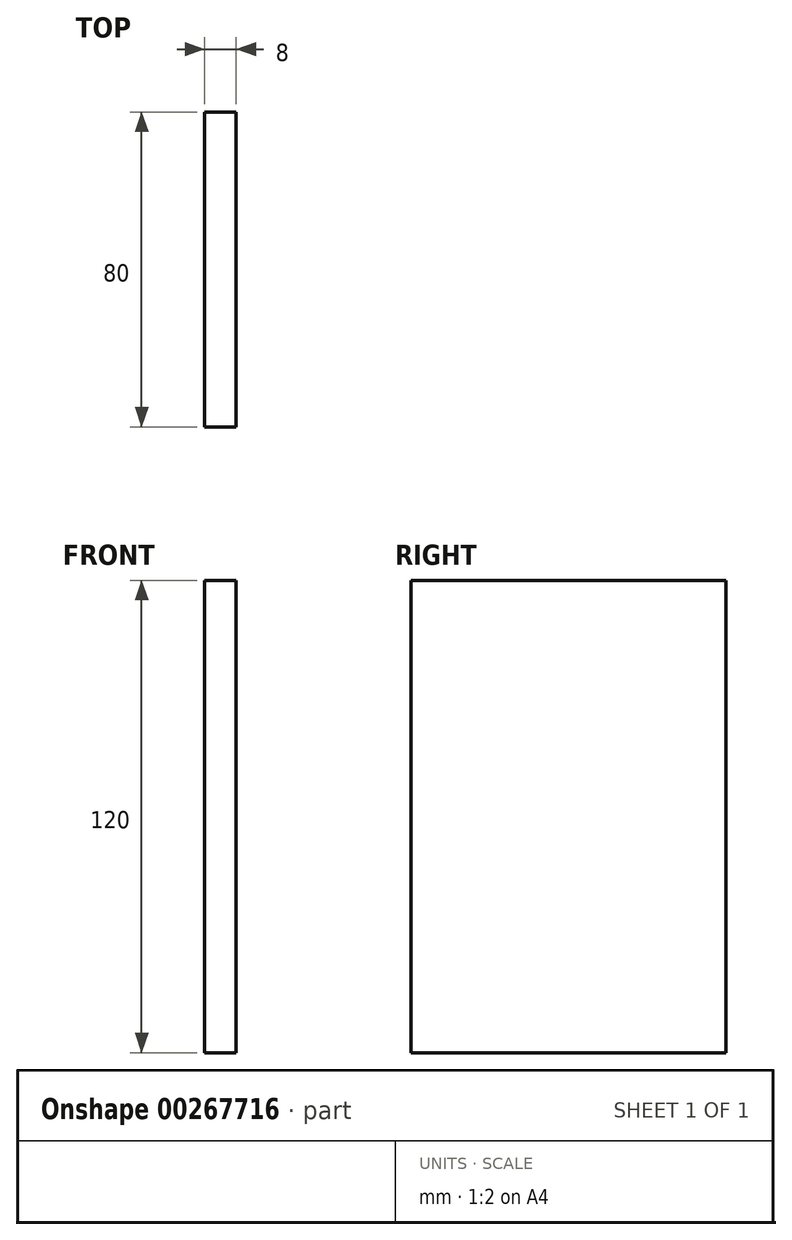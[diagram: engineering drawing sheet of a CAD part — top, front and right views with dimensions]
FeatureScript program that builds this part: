
annotation { "Feature Type Name" : "Feature", "Feature Type Description" : "" }
export const myFeature = defineFeature(function(context is Context, id is Id, definition is map)
    precondition{}
    {
        {
            var Q0;
            Q0=qCreatedBy(makeId("Front.planeOp"),FACE);
            var sketch = newSketch(context, id + "F0", { "sketchPlane" : qUnion([Q0])});
            skLineSegment(sketch, "E0.bottom", {"start": v(-4, 60) * mm, "end": v(4, 60) * mm});
            skLineSegment(sketch, "E0.top", {"start": v(-4, -60) * mm, "end": v(4, -60) * mm});
            skLineSegment(sketch, "E0.left", {"start": v(-4, 60) * mm, "end": v(-4, -60) * mm});
            skLineSegment(sketch, "E0.right", {"start": v(4, 60) * mm, "end": v(4, -60) * mm});
            skPoint(sketch, "E0.middle", {"position": v(0, 0) * mm});
            skSolve(sketch);
        }
        {
            var Q0;
            Q0 = qSketchRegion(id + "F0", true);
            extrude(context, id + "F1", {"entities" : qUnion([Q0]), "oppositeDirection" : true, "depth" : 80 * mm});
        }
    });
